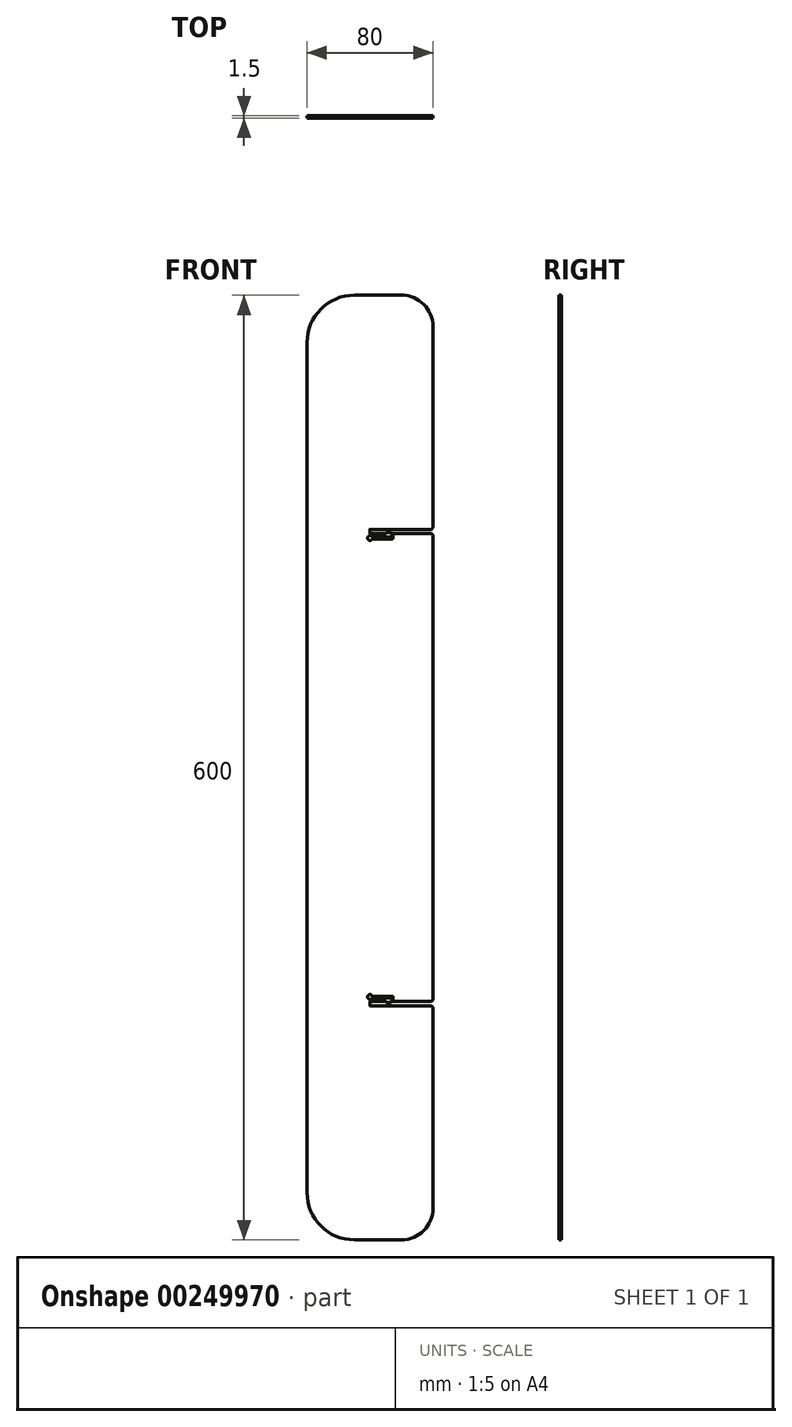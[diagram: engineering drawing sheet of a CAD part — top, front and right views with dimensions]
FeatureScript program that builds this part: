
annotation { "Feature Type Name" : "Feature", "Feature Type Description" : "" }
export const myFeature = defineFeature(function(context is Context, id is Id, definition is map)
    precondition{}
    {
        {
            var Q0;
            Q0=qCreatedBy(makeId("Front.planeOp"),FACE);
            var sketch = newSketch(context, id + "F0", { "sketchPlane" : qUnion([Q0])});
            skLineSegment(sketch, "E0.0", {"start": v(40, 430) * mm, "end": v(40, 302.27) * mm});
            skLineSegment(sketch, "E1.0", {"start": v(0.1, 1.27) * mm, "end": v(3, 1.27) * mm});
            skLineSegment(sketch, "E2.0", {"start": v(3.2, 1.47) * mm, "end": v(9.8, 1.47) * mm});
            skArc(sketch, "E3.0.0", {"start": v(1.41, 3.75) * mm, "mid": v(0.87, 3.03) * mm, "end": v(0, 2.75) * mm});
            skLineSegment(sketch, "E3.0.3", {"start": v(3, 1.27) * mm, "end": v(3.2, 1.47) * mm});
            skLineSegment(sketch, "E3.0.7", {"start": v(10.13, 0.78) * mm, "end": v(13.05, 0.78) * mm});
            skLineSegment(sketch, "E4.0.6", {"start": v(9.99, 1.33) * mm, "end": v(10.13, 0.78) * mm});
            skArc(sketch, "E4.0.8", {"start": v(13.05, 0.78) * mm, "mid": v(13.13, 0.8) * mm, "end": v(13.2, 0.83) * mm});
            skLineSegment(sketch, "E4.0.9", {"start": v(13.2, 0.83) * mm, "end": v(13.94, 1.58) * mm});
            skLineSegment(sketch, "E4.0.11", {"start": v(14, 1.72) * mm, "end": v(14, 3.55) * mm});
            skLineSegment(sketch, "E4.0.13", {"start": v(13.8, 3.75) * mm, "end": v(1.41, 3.75) * mm});
            skArc(sketch, "E5.0.5", {"start": v(9.8, 1.47) * mm, "mid": v(9.91, 1.43) * mm, "end": v(9.99, 1.33) * mm});
            skArc(sketch, "E5.0.10", {"start": v(13.94, 1.58) * mm, "mid": v(13.98, 1.65) * mm, "end": v(14, 1.72) * mm});
            skArc(sketch, "E6.0.6", {"start": v(14.5, 1.47) * mm, "mid": v(14.56, 1.33) * mm, "end": v(14.7, 1.28) * mm});
            skLineSegment(sketch, "E6.0.13", {"start": v(40, -130) * mm, "end": v(40, -2.27) * mm});
            skLineSegment(sketch, "E6.0.15", {"start": v(39, -1.28) * mm, "end": v(0.1, -1.28) * mm});
            skLineSegment(sketch, "E7.0.0", {"start": v(0, 0) * mm, "end": v(0, 1.17) * mm});
            skLineSegment(sketch, "E7.0.7", {"start": v(14.7, 1.28) * mm, "end": v(39, 1.28) * mm});
            skLineSegment(sketch, "E7.0.14", {"start": v(40, -2.27) * mm, "end": v(39, -1.27) * mm});
            skLineSegment(sketch, "E7.0.16", {"start": v(0, -1.18) * mm, "end": v(0, 0) * mm});
            skArc(sketch, "E8.0.2", {"start": v(0, 2.75) * mm, "mid": v(-1.22, 5.12) * mm, "end": v(1.41, 4.75) * mm});
            skLineSegment(sketch, "E8.0.3", {"start": v(1.41, 4.75) * mm, "end": v(14.3, 4.75) * mm});
            skLineSegment(sketch, "E8.0.5", {"start": v(14.5, 4.55) * mm, "end": v(14.5, 1.47) * mm});
            skLineSegment(sketch, "E9", {"start": v(-4.63, 0) * mm, "end": v(42.86, 0) * mm, "construction": true});
            skPoint(sketch, "E10", {"position": v(10, 1.28) * mm});
            skLineSegment(sketch, "E11", {"start": v(-40, -120) * mm, "end": v(-40, 420) * mm});
            skLineSegment(sketch, "E12", {"start": v(-47.13, 150) * mm, "end": v(59.8, 150) * mm, "construction": true});
            skLineSegment(sketch, "E13", {"start": v(-10, -150) * mm, "end": v(20, -150) * mm});
            skLineSegment(sketch, "E14.MirrorCS", {"start": v(-10, 450) * mm, "end": v(20, 450) * mm});
            skLineSegment(sketch, "E15.trimOffspring", {"start": v(40, 297.73) * mm, "end": v(40, 2.28) * mm});
            skPoint(sketch, "E16.visualSharp", {"position": v(-40, 450) * mm});
            skArc(sketch, "E16.filletArc", {"start": v(-10, 450) * mm, "mid": v(-31.21, 441.21) * mm, "end": v(-40, 420) * mm});
            skPoint(sketch, "E17.visualSharp", {"position": v(-40, -150) * mm});
            skArc(sketch, "E17.filletArc", {"start": v(-40, -120) * mm, "mid": v(-31.21, -141.21) * mm, "end": v(-10, -150) * mm});
            skPoint(sketch, "E18.visualSharp", {"position": v(40, -150) * mm});
            skArc(sketch, "E18.filletArc", {"start": v(20, -150) * mm, "mid": v(34.14, -144.14) * mm, "end": v(40, -130) * mm});
            skPoint(sketch, "E19.visualSharp", {"position": v(40, 450) * mm});
            skArc(sketch, "E19.filletArc", {"start": v(40, 430) * mm, "mid": v(34.14, 444.14) * mm, "end": v(20, 450) * mm});
            skArc(sketch, "E20", {"start": v(0.1, 1.27) * mm, "mid": v(-0.07, 1.35) * mm, "end": v(0, 1.17) * mm});
            skArc(sketch, "E21", {"start": v(0, -1.18) * mm, "mid": v(-0.07, -1.35) * mm, "end": v(0.1, -1.28) * mm});
            skPoint(sketch, "E22.orphan", {"position": v(0, 0.75) * mm});
            skLineSegment(sketch, "E23", {"start": v(0, 6.6) * mm, "end": v(0, -2.3) * mm, "construction": true});
            skPoint(sketch, "E24", {"position": v(0, 0) * mm});
            skCircle(sketch, "E25", {"center": v(0, 0) * mm, "radius": 1.27 * mm, "construction": true});
            skLineSegment(sketch, "E26.MirrorCS", {"start": v(40, 2.27) * mm, "end": v(39, 1.28) * mm});
            skPoint(sketch, "E27.newPointA", {"position": v(14.3, 4.75) * mm});
            skArc(sketch, "E27.filletArc", {"start": v(14.5, 4.55) * mm, "mid": v(14.44, 4.7) * mm, "end": v(14.3, 4.75) * mm});
            skPoint(sketch, "E28.newPointA", {"position": v(13.8, 3.75) * mm});
            skArc(sketch, "E28.filletArc", {"start": v(14, 3.55) * mm, "mid": v(13.94, 3.7) * mm, "end": v(13.8, 3.75) * mm});
            skArc(sketch, "E29.MirrorCS", {"start": v(0.1, 298.73) * mm, "mid": v(-0.07, 298.65) * mm, "end": v(0, 298.82) * mm});
            skArc(sketch, "E30.MirrorCS", {"start": v(0, 301.18) * mm, "mid": v(-0.07, 301.35) * mm, "end": v(0.1, 301.28) * mm});
            skCircle(sketch, "E31.MirrorC", {"center": v(0, 300) * mm, "radius": 1.27 * mm, "construction": true});
            skArc(sketch, "E32.MirrorCS", {"start": v(14, 296.45) * mm, "mid": v(13.94, 296.3) * mm, "end": v(13.8, 296.25) * mm});
            skLineSegment(sketch, "E33.MirrorCS", {"start": v(0, 300) * mm, "end": v(0, 298.82) * mm});
            skLineSegment(sketch, "E34.MirrorCS", {"start": v(0, 301.17) * mm, "end": v(0, 300) * mm});
            skArc(sketch, "E35.MirrorCS", {"start": v(14.5, 295.45) * mm, "mid": v(14.44, 295.3) * mm, "end": v(14.3, 295.25) * mm});
            skLineSegment(sketch, "E36.MirrorCS", {"start": v(14.5, 295.45) * mm, "end": v(14.5, 298.52) * mm});
            skLineSegment(sketch, "E37.MirrorCS", {"start": v(14, 298.28) * mm, "end": v(14, 296.45) * mm});
            skArc(sketch, "E38.MirrorCS", {"start": v(9.8, 298.52) * mm, "mid": v(9.91, 298.57) * mm, "end": v(9.99, 298.67) * mm});
            skLineSegment(sketch, "E39.MirrorCS", {"start": v(9.99, 298.67) * mm, "end": v(10.13, 299.22) * mm});
            skLineSegment(sketch, "E40.MirrorCS", {"start": v(0.1, 298.73) * mm, "end": v(3, 298.73) * mm});
            skLineSegment(sketch, "E41.MirrorCS", {"start": v(10.13, 299.22) * mm, "end": v(13.05, 299.22) * mm});
            skArc(sketch, "E42.MirrorCS", {"start": v(14.5, 298.52) * mm, "mid": v(14.56, 298.67) * mm, "end": v(14.7, 298.72) * mm});
            skLineSegment(sketch, "E43.MirrorCS", {"start": v(13.2, 299.17) * mm, "end": v(13.94, 298.42) * mm});
            skLineSegment(sketch, "E44.MirrorCS", {"start": v(3, 298.72) * mm, "end": v(3.2, 298.52) * mm});
            skArc(sketch, "E45.MirrorCS", {"start": v(13.05, 299.22) * mm, "mid": v(13.13, 299.2) * mm, "end": v(13.2, 299.17) * mm});
            skArc(sketch, "E46.MirrorCS", {"start": v(13.94, 298.42) * mm, "mid": v(13.98, 298.35) * mm, "end": v(14, 298.28) * mm});
            skArc(sketch, "E47.MirrorCS", {"start": v(1.41, 296.25) * mm, "mid": v(0.87, 296.97) * mm, "end": v(0, 297.25) * mm});
            skLineSegment(sketch, "E48.MirrorCS", {"start": v(40, 302.27) * mm, "end": v(39, 301.27) * mm});
            skLineSegment(sketch, "E49.MirrorCS", {"start": v(0, 293.4) * mm, "end": v(0, 302.3) * mm, "construction": true});
            skLineSegment(sketch, "E50.MirrorCS", {"start": v(40, 297.73) * mm, "end": v(39, 298.73) * mm});
            skLineSegment(sketch, "E51.MirrorCS", {"start": v(3.2, 298.52) * mm, "end": v(9.8, 298.52) * mm});
            skPoint(sketch, "E52.MirrorP", {"position": v(0, 299.25) * mm});
            skPoint(sketch, "E53.MirrorP", {"position": v(14.3, 295.25) * mm});
            skLineSegment(sketch, "E54.MirrorCS", {"start": v(-4.63, 300) * mm, "end": v(42.86, 300) * mm, "construction": true});
            skLineSegment(sketch, "E55.MirrorCS", {"start": v(14.7, 298.72) * mm, "end": v(39, 298.72) * mm});
            skArc(sketch, "E56.MirrorCS", {"start": v(0, 297.25) * mm, "mid": v(-1.22, 294.88) * mm, "end": v(1.41, 295.25) * mm});
            skPoint(sketch, "E57.MirrorP", {"position": v(10, 298.72) * mm});
            skLineSegment(sketch, "E58.MirrorCS", {"start": v(39, 301.28) * mm, "end": v(0.1, 301.28) * mm});
            skPoint(sketch, "E59.MirrorP", {"position": v(13.8, 296.25) * mm});
            skLineSegment(sketch, "E60.MirrorCS", {"start": v(13.8, 296.25) * mm, "end": v(1.41, 296.25) * mm});
            skLineSegment(sketch, "E61.MirrorCS", {"start": v(1.41, 295.25) * mm, "end": v(14.3, 295.25) * mm});
            skSolve(sketch);
        }
        {
            var Q0;
            Q0 = qSketchRegion(id + "F0", true);
            extrude(context, id + "F1", {"entities" : qUnion([Q0]), "depth" : 0.75 * mm, "hasSecondDirection" : true, "secondDirectionOppositeDirection" : true, "secondDirectionDepth" : 0.75 * mm});
        }
    });
